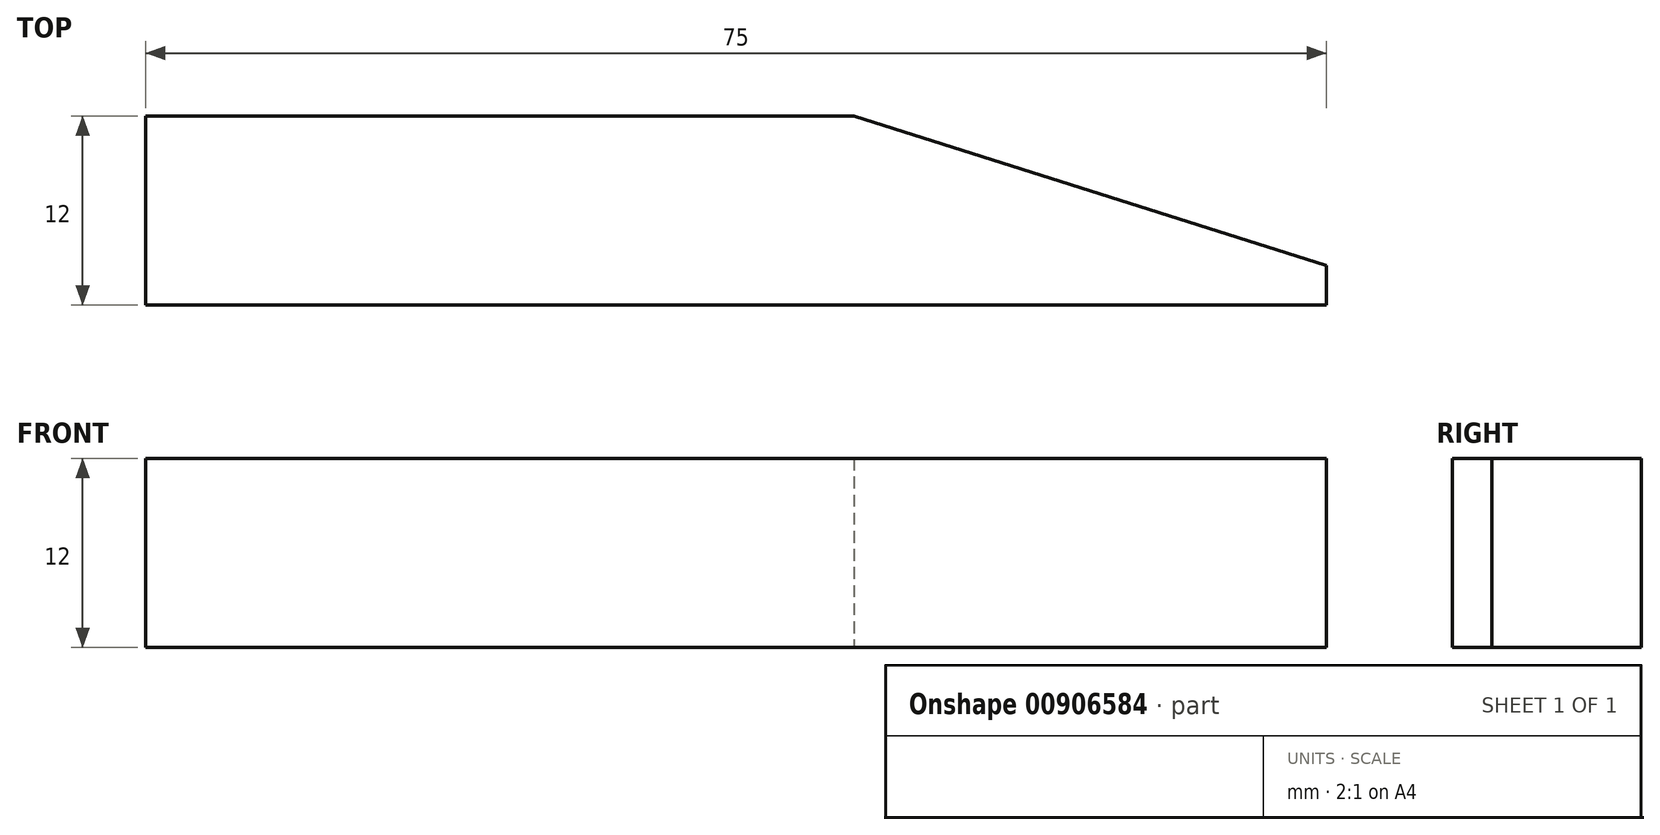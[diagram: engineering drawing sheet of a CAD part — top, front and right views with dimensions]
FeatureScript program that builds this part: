
annotation { "Feature Type Name" : "Feature", "Feature Type Description" : "" }
export const myFeature = defineFeature(function(context is Context, id is Id, definition is map)
    precondition{}
    {
        {
            var Q0;
            Q0=qCreatedBy(makeId("Top.planeOp"),FACE);
            var sketch = newSketch(context, id + "F0", { "sketchPlane" : qUnion([Q0])});
            skLineSegment(sketch, "E0", {"start": v(-21.5, 0) * mm, "end": v(-21.5, 12) * mm});
            skLineSegment(sketch, "E1", {"start": v(-21.5, 12) * mm, "end": v(23.5, 12) * mm});
            skLineSegment(sketch, "E2", {"start": v(23.5, 12) * mm, "end": v(53.5, 2.5) * mm});
            skLineSegment(sketch, "E3", {"start": v(53.5, 2.5) * mm, "end": v(53.5, 0) * mm});
            skLineSegment(sketch, "E4", {"start": v(-21.5, 0) * mm, "end": v(53.5, 0) * mm});
            skSolve(sketch);
        }
        {
            var Q0;
            Q0 = qSketchRegion(id + "F0", true);
            extrude(context, id + "F1", {"entities" : qUnion([Q0]), "depth" : 12 * mm, "offsetDistance" : 25 * mm});
        }
    });
